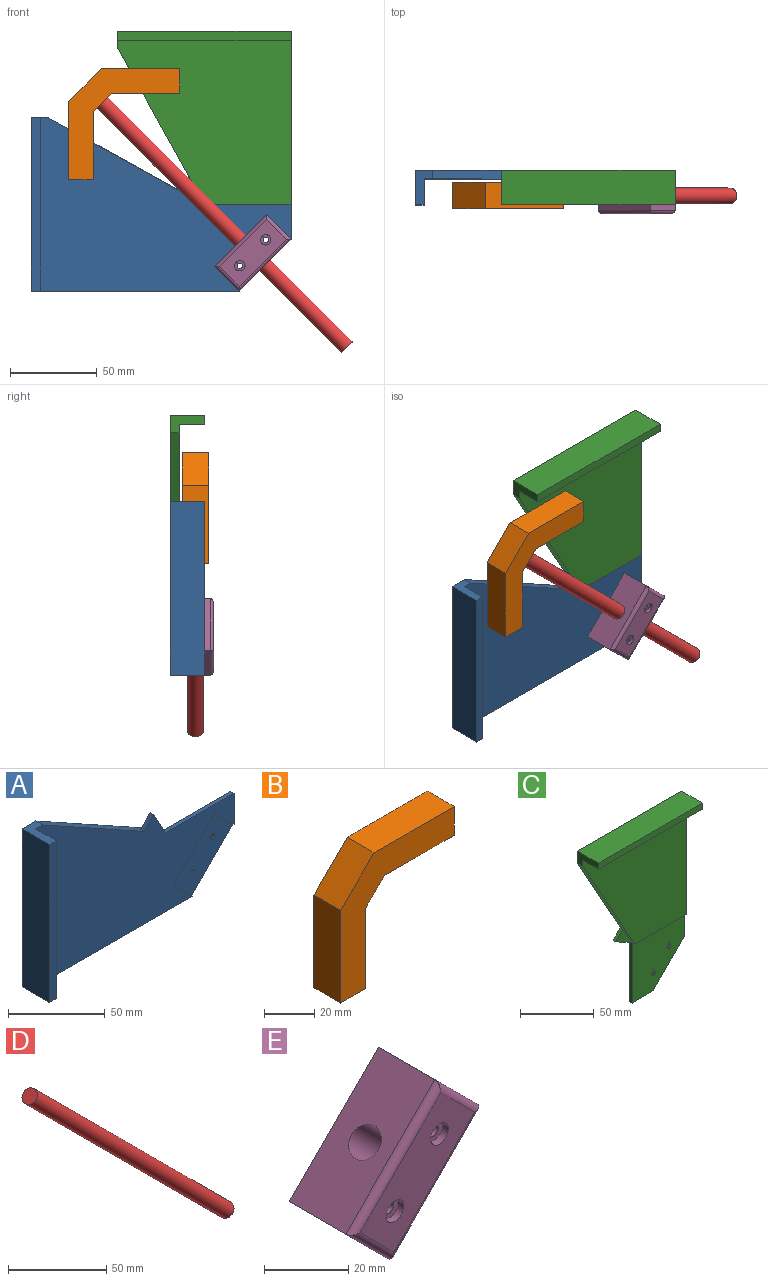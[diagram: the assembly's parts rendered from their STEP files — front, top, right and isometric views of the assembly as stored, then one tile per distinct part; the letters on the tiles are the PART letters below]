
ASSEMBLY  parts=5 mates=4
PART A: 22 faces, bbox 150x20x100 mm
  f0: plane 30x30mm, normal (0.71,0,-0.71), area 63.6mm2, adj f4,f11,f12,f19
  f1: plane 145x100mm, normal (0,-1,0), area 8530.7mm2, adj f2,f4,f5,f7,f10,f11,f14,f15
  f2: plane 90x50mm, normal (0.49,0,0.87), area 469.3mm2, adj f1,f3,f5,f6,f13,f14
  f3: plane 50x2.5mm, normal (1,0,0), area 125mm2, adj f2,f4,f6,f12
  f4: plane 120x20mm, normal (0,0,-1), area 624.9mm2, adj f0,f1,f3,f6,f7,f8,f9,f12
  f5: plane 20x10mm, normal (0,0,1), area 125mm2, adj f1,f2,f6,f7,f8,f9
  f6: plane 100x100mm, normal (0,1,0), area 7750mm2, adj f2,f3,f4,f5,f8
  f7: plane 100x15mm, normal (1,0,0), area 1500mm2, adj f1,f4,f5,f9
  f8: plane 100x20mm, normal (-1,0,0), area 2000mm2, adj f4,f5,f6,f9
  f9: plane 100x5mm, normal (0,-1,0), area 500mm2, adj f4,f5,f7,f8
  f10: plane 50x2.5mm, normal (0,0,1), area 125mm2, adj f1,f11,f12,f15
  f11: plane 20x2.5mm, normal (1,0,0), area 49.9mm2, adj f0,f1,f10,f12,f17,f19
  f12: plane 50x50mm, normal (0,1,0), area 2033.9mm2, adj f0,f3,f4,f10,f11,f20,f21
  f13: plane 15.91x15.91mm, normal (0,1,0), area 87.5mm2, adj f2,f14,f15
  f14: plane 7.07x7.07mm, normal (-0.71,0,0.71), area 25mm2, adj f1,f2,f13,f15
  f15: plane 15.91x8.84mm, normal (0.87,0,0.49), area 45.5mm2, adj f1,f10,f13,f14
  f16: plane 14.14x14.14mm, normal (0.71,0,0.71), area 20mm2, adj f1,f4,f18,f19
  f17: plane 14.14x14.14mm, normal (-0.71,0,-0.71), area 20mm2, adj f1,f11,f18,f19
  f18: plane 30.14x30.14mm, normal (0.71,0,-0.71), area 42.6mm2, adj f1,f16,f17,f19
  f19: plane 44.28x44.28mm, normal (0,-1,0), area 840.7mm2, adj f0,f4,f11,f16,f17,f18,f20,f21
  f20: cylinder r=1.6mm len=3.2mm, axis (0,-1,0), area 15.1mm2, adj f12,f19
  f21: cylinder r=1.6mm len=3.2mm, axis (0,-1,0), area 15.1mm2, adj f12,f19
PART B: 12 faces, bbox 64.1x15.1x64.1 mm
  f0: plane 45.25x15.1mm, normal (0,0,1), area 683.3mm2, adj f1,f7,f8,f9
  f1: plane 18.89x18.89mm, normal (-0.71,0,0.71), area 403.4mm2, adj f0,f2,f8,f9
  f2: plane 45.25x15.1mm, normal (-1,0,0), area 683.3mm2, adj f1,f3,f8,f9
  f3: plane 15.1x14.14mm, normal (0,0,-1), area 213.5mm2, adj f2,f4,f8,f9
  f4: plane 39.39x15.1mm, normal (1,0,0), area 594.8mm2, adj f3,f5,f8,f9
  f5: plane 15.1x10.61mm, normal (0.71,0,-0.71), area 162.9mm2, adj f4,f6,f8,f9,f11
  f6: plane 39.39x15.1mm, normal (0,0,-1), area 594.8mm2, adj f5,f7,f8,f9
  f7: plane 15.1x14.14mm, normal (1,0,0), area 213.5mm2, adj f0,f6,f8,f9
  f8: plane 64.14x64.14mm, normal (0,-1,0), area 1492mm2, adj f0,f1,f2,f3,f4,f5,f6,f7
  f9: plane 64.14x64.14mm, normal (0,1,0), area 1492mm2, adj f0,f1,f2,f3,f4,f5,f6,f7
  f10: cone r=0mm half-angle=59deg, axis (0.71,0,-0.71), area 74.2mm2, adj f11
  f11: cylinder r=4.5mm len=9.9mm, axis (0.71,0,-0.71), area 141.4mm2, adj f5,f10
PART C: 32 faces, bbox 100x20x150 mm
  f0: cylinder r=1.6mm len=3.2mm, axis (0,-1,0), area 5mm2, adj f11,f31
  f1: cylinder r=1.6mm len=3.2mm, axis (0,-1,0), area 5mm2, adj f11,f24
  f2: plane 90x50mm, normal (-0.87,0,-0.49), area 469.3mm2, adj f4,f5,f6,f7,f12,f14
  f3: plane 120x20mm, normal (1,0,0), area 625mm2, adj f5,f6,f7,f10,f11,f15,f16,f17
  f4: plane 20x10mm, normal (-1,0,0), area 125mm2, adj f2,f6,f7,f15,f16,f17
  f5: plane 50x2.5mm, normal (0,0,-1), area 125mm2, adj f2,f3,f6,f11
  f6: plane 100x95mm, normal (0,-1,0), area 7250mm2, adj f2,f3,f4,f5,f15
  f7: plane 150x100mm, normal (0,1,0), area 9831.2mm2, adj f2,f3,f4,f8,f9,f10,f12,f13
  f8: plane 50x2.5mm, normal (-1,0,0), area 125mm2, adj f7,f9,f11,f13
  f9: plane 20x2.5mm, normal (0,0,-1), area 50mm2, adj f7,f8,f10,f11
  f10: plane 30x30mm, normal (0.71,0,-0.71), area 106.1mm2, adj f3,f7,f9,f11
  f11: plane 50x50mm, normal (0,-1,0), area 2033.9mm2, adj f0,f1,f3,f5,f8,f9,f10
  f12: plane 7.07x7.07mm, normal (-0.71,0,0.71), area 25mm2, adj f2,f7,f13,f14
  f13: plane 15.91x8.84mm, normal (-0.49,0,-0.87), area 45.5mm2, adj f7,f8,f12,f14
  f14: plane 15.91x15.91mm, normal (0,-1,0), area 87.5mm2, adj f2,f12,f13
  f15: plane 100x15mm, normal (0,0,-1), area 1500mm2, adj f3,f4,f6,f17
  f16: plane 100x20mm, normal (0,0,1), area 2000mm2, adj f3,f4,f7,f17
  f17: plane 100x5mm, normal (0,-1,0), area 500mm2, adj f3,f4,f15,f16
  f18: plane 3.26x2mm, normal (-0.99,0,-0.14), area 6.6mm2, adj f7,f19,f23,f24
  f19: plane 2.6x2.02mm, normal (-0.61,0,0.79), area 6.6mm2, adj f7,f18,f20,f24
  f20: plane 3.05x2mm, normal (0.38,0,0.93), area 6.6mm2, adj f7,f19,f21,f24
  f21: plane 3.26x2mm, normal (0.99,0,0.14), area 6.6mm2, adj f7,f20,f22,f24
  f22: plane 2.6x2.02mm, normal (0.61,0,-0.79), area 6.6mm2, adj f7,f21,f23,f24
  f23: plane 3.05x2mm, normal (-0.38,0,-0.93), area 6.6mm2, adj f7,f18,f22,f24
  f24: plane 6.52x6.1mm, normal (0,1,0), area 20.1mm2, adj f1,f18,f19,f20,f21,f22,f23
  f25: plane 3.18x2mm, normal (-0.97,0,-0.26), area 6.6mm2, adj f7,f26,f30,f31
  f26: plane 2.33x2.33mm, normal (-0.71,0,0.71), area 6.6mm2, adj f7,f25,f27,f31
  f27: plane 3.18x2mm, normal (0.26,0,0.97), area 6.6mm2, adj f7,f26,f28,f31
  f28: plane 3.18x2mm, normal (0.97,0,0.26), area 6.6mm2, adj f7,f27,f29,f31
  f29: plane 2.33x2.33mm, normal (0.71,0,-0.71), area 6.6mm2, adj f7,f28,f30,f31
  f30: plane 3.18x2mm, normal (-0.26,0,-0.97), area 6.6mm2, adj f7,f25,f29,f31
  f31: plane 6.36x6.36mm, normal (0,1,0), area 20.1mm2, adj f0,f25,f26,f27,f28,f29,f30
PART D: 3 faces, bbox 147.8x9x147.8 mm
  f0: cylinder r=4.5mm len=147.79mm, axis (-0.71,0,0.71), area 5654.9mm2, adj f1,f2
  f1: plane 9x6.36mm, normal (0.71,0,-0.71), area 63.6mm2, adj f0
  f2: plane 9x6.36mm, normal (-0.71,0,0.71), area 63.6mm2, adj f0
PART E: 17 faces, bbox 44.1x21x44.1 mm
  f0: plane 19x14.14mm, normal (-0.71,0,-0.71), area 380mm2, adj f1,f3,f5,f7
  f1: plane 30x30mm, normal (0.71,0,-0.71), area 742.5mm2, adj f0,f2,f5,f6,f9
  f2: plane 19x14.14mm, normal (0.71,0,0.71), area 380mm2, adj f1,f3,f5,f10
  f3: plane 30x30mm, normal (-0.71,0,0.71), area 742.5mm2, adj f0,f2,f5,f6,f8
  f4: plane 38.49x38.49mm, normal (0,-1,0), area 558.3mm2, adj f7,f8,f9,f10,f13,f16
  f5: plane 44.14x44.14mm, normal (0,1,0), area 832.4mm2, adj f0,f1,f2,f3,f11,f14
  f6: cylinder r=4.5mm len=20.51mm, axis (0.71,0,-0.71), area 565.5mm2, adj f1,f3
  f7: cylinder r=2mm len=15.56mm, axis (-0.71,0,0.71), area 58.3mm2, adj f0,f4,f8,f9
  f8: cylinder r=2mm len=31.41mm, axis (0.71,0,0.71), area 128.7mm2, adj f3,f4,f7,f10
  f9: cylinder r=2mm len=31.41mm, axis (-0.71,0,-0.71), area 128.7mm2, adj f1,f4,f7,f10
  f10: cylinder r=2mm len=15.56mm, axis (0.71,0,-0.71), area 58.3mm2, adj f2,f4,f8,f9
  f11: cylinder r=1.6mm len=19mm, axis (0,-1,0), area 191mm2, adj f5,f12
  f12: plane 6x6mm, normal (0,-1,0), area 20.2mm2, adj f11,f13
  f13: cylinder r=3mm len=6mm, axis (0,-1,0), area 37.7mm2, adj f4,f12
  f14: cylinder r=1.6mm len=19mm, axis (0,-1,0), area 191mm2, adj f5,f15
  f15: plane 6x6mm, normal (0,-1,0), area 20.2mm2, adj f14,f16
  f16: cylinder r=3mm len=6mm, axis (0,-1,0), area 37.7mm2, adj f4,f15
PLACE A at identity
PLACE B t=(35.66,-2.05,-35.66)mm
PLACE C at identity fixed
PLACE D t=(-35.05,0,35.05)mm
PLACE E at identity
MATE fastened E.f14 <-> A.f21  axis (0,1,0) through (60.43,-4,-45.43)mm
MATE fastened D.f0 <-> B.f10  axis (-0.71,0,0.71) through (-34.04,-14.5,34.04)mm
MATE slider D.f0 <-> E.f6  axis (-0.71,0,0.71) through (36.67,-14.5,-36.67)mm
MATE fastened A.f21 <-> C.f1  axis (0,1,0) through (60.43,-2.5,-45.43)mm
